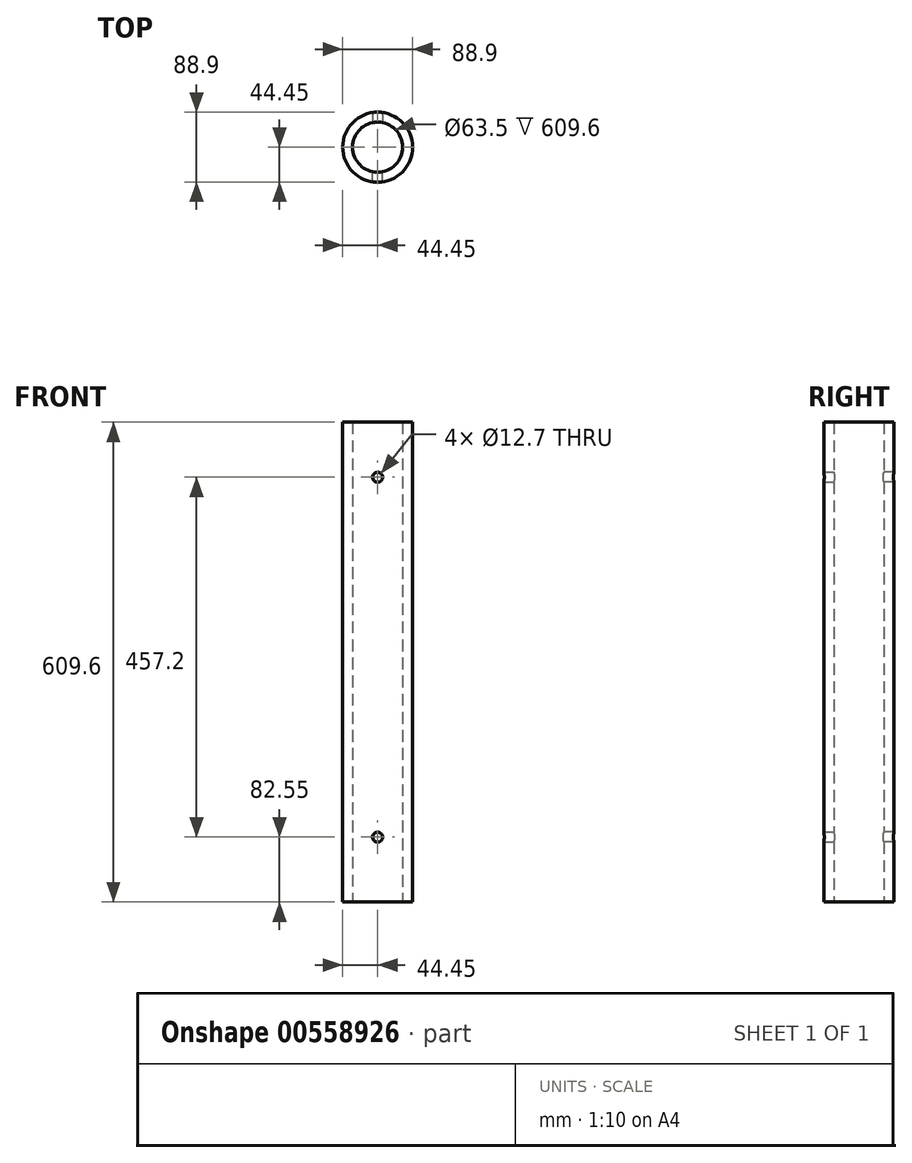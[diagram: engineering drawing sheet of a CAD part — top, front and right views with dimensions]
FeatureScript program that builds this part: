
annotation { "Feature Type Name" : "Feature", "Feature Type Description" : "" }
export const myFeature = defineFeature(function(context is Context, id is Id, definition is map)
    precondition{}
    {
        {
            var Q0;
            Q0=qCreatedBy(makeId("Top.planeOp"),FACE);
            var sketch = newSketch(context, id + "F0", { "sketchPlane" : qUnion([Q0])});
            skCircle(sketch, "E0", {"center": v(0, 0) * mm, "radius": 44.45 * mm});
            skCircle(sketch, "E1", {"center": v(0, 0) * mm, "radius": 31.75 * mm});
            skSolve(sketch);
        }
        {
            var Q0;
            Q0=makeQuery(id+"F0.imprint","IMPRINT",FACE,{"disambiguationData":[TD([[makeQuery(id+"F0.imprint","IMPRINT",EDGE,{"derivedFrom":sQuery(id+"F0.wireOp",EDGE,"E0")}),1.0]])]});
            extrude(context, id + "F1", {"entities" : qUnion([Q0]), "depth" : 609.6 * mm, "offsetDistance" : 25.4 * mm});
        }
        {
            var Q0;
            Q0=qCreatedBy(makeId("Front.planeOp"),FACE);
            var sketch = newSketch(context, id + "F2", { "sketchPlane" : qUnion([Q0])});
            skCircle(sketch, "E2", {"center": v(0, 539.75) * mm, "radius": 6.35 * mm});
            skCircle(sketch, "E3.0.1.0", {"center": v(0, 82.55) * mm, "radius": 6.35 * mm});
            skLineSegment(sketch, "E3.direction1", {"start": v(0, 539.75) * mm, "end": v(25.4, 539.75) * mm, "construction": true});
            skLineSegment(sketch, "E3.direction2", {"start": v(0, 539.75) * mm, "end": v(0, 82.55) * mm, "construction": true});
            skSolve(sketch);
        }
        {
            var Q0;
            Q0 = qSketchRegion(id + "F2", true);
            extrude(context, id + "F3", {"entities" : qUnion([Q0]), "operationType" : NewBodyOperationType.REMOVE, "endBound" : BoundingType.THROUGH_ALL, "depth" : 25.4 * mm, "offsetDistance" : 25.4 * mm});
        }
        {
            var Q0;
            Q0 = qSketchRegion(id + "F2", true);
            extrude(context, id + "F4", {"entities" : qUnion([Q0]), "operationType" : NewBodyOperationType.REMOVE, "endBound" : BoundingType.THROUGH_ALL, "oppositeDirection" : true, "depth" : 25.4 * mm, "offsetDistance" : 25.4 * mm});
        }
    });
